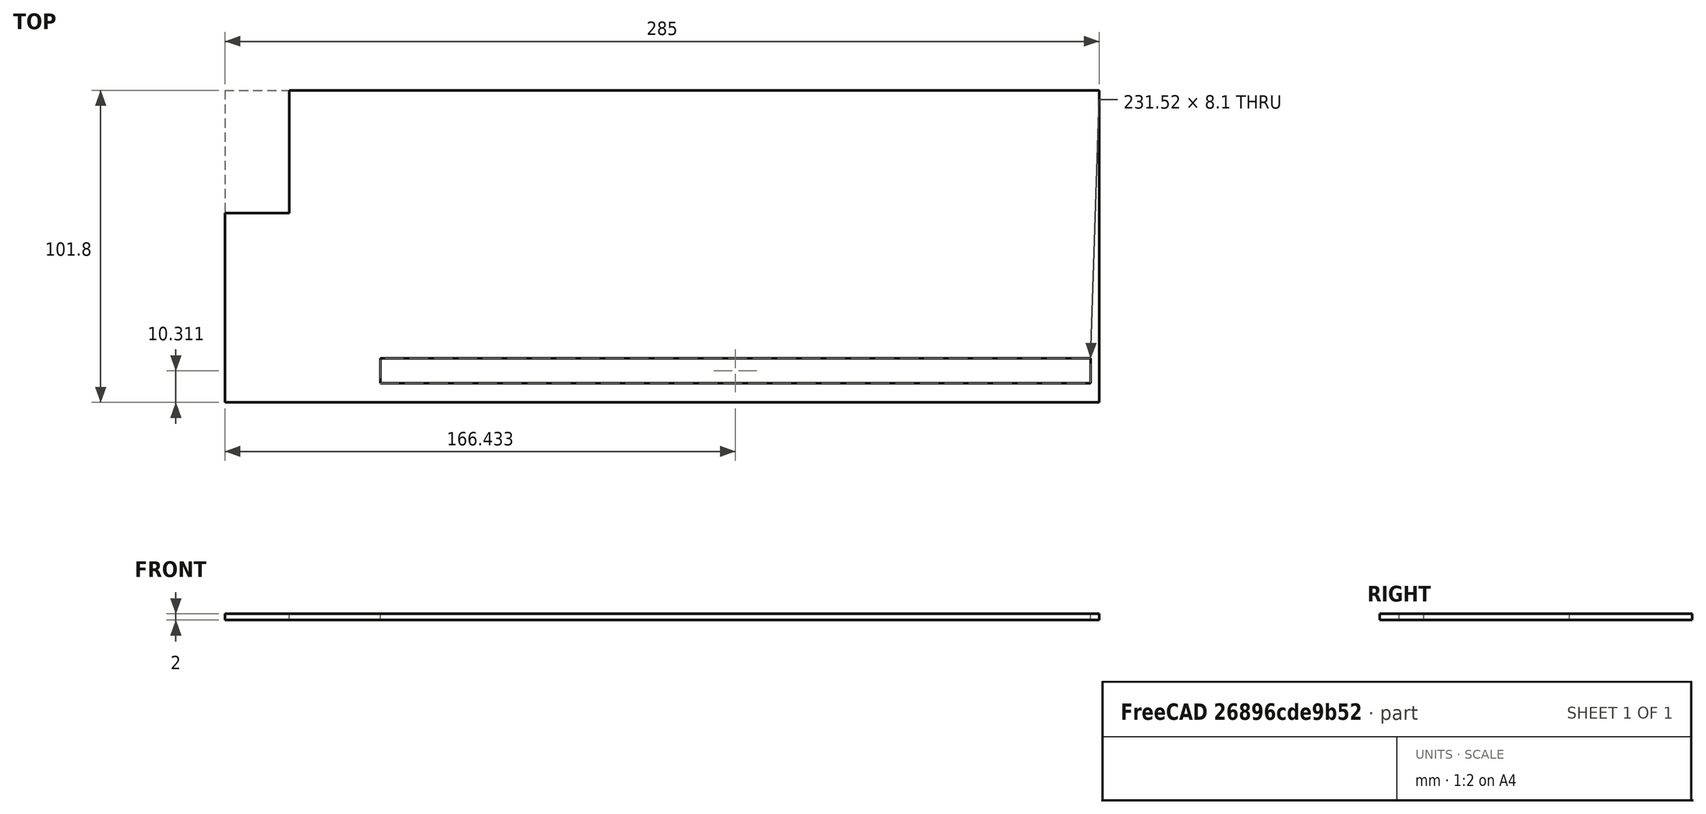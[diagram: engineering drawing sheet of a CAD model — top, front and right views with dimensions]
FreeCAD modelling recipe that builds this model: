
FCSTD DOCUMENT  (FreeCAD 0.20R29603 (Git))
Label: TopPanel
License: All rights reserved
LicenseURL: http://en.wikipedia.org/wiki/All_rights_reserved
objects: Sketcher::SketchObject×1, PartDesign::Pad×1, PartDesign::Body×1
note: 4 computed .brp shape members not serialized (recipe doc carries the construction recipe); baked Part::Feature solids carry a one-line shape summary decoded from their .brp

FEATURE [Sketcher::SketchObject] Sketch
  FullyConstrained = false
  MapMode = 5
  Support = -> [XY_Plane001]
  sketch-geometry (12):
    g0: LineSegment StartX=50.6712 StartY=6.26253 StartZ=0 EndX=50.6757 EndY=14.3625 EndZ=0
    g1: LineSegment StartX=50.6757 StartY=14.3625 StartZ=0 EndX=282.196 EndY=14.3634 EndZ=0
    g2: LineSegment StartX=282.196 StartY=14.3634 StartZ=0 EndX=282.196 EndY=6.25873 EndZ=0
    g3: LineSegment StartX=282.196 StartY=6.25873 StartZ=0 EndX=50.6712 EndY=6.26253 EndZ=0
    g4: LineSegment StartX=2.21647e-09 StartY=101.8 StartZ=0 EndX=21 EndY=101.8 EndZ=0
    g5: LineSegment StartX=21 StartY=101.8 StartZ=0 EndX=21 EndY=61.8 EndZ=0
    g6: LineSegment StartX=21 StartY=61.8 StartZ=0 EndX=2.21647e-09 EndY=61.8 EndZ=0
    g7: LineSegment StartX=2.21647e-09 StartY=61.8 StartZ=0 EndX=2.21647e-09 EndY=101.8 EndZ=0
    g8: LineSegment StartX=0 StartY=0 StartZ=0 EndX=285 EndY=0 EndZ=0
    g9: LineSegment StartX=285 StartY=0 StartZ=0 EndX=285 EndY=101.8 EndZ=0
    g10: LineSegment StartX=285 StartY=101.8 StartZ=0 EndX=0 EndY=101.8 EndZ=0
    g11: LineSegment StartX=0 StartY=101.8 StartZ=0 EndX=0 EndY=0 EndZ=0
  constraints (25):
    c: DistanceY(g0,g0) = 8.1
    c: DistanceX(g1,g1) = 231.52
    c: Coincident(g1,g0)
    c: Coincident(g0,g3)
    c: Coincident(g4,g5)
    c: Coincident(g5,g6)
    c: Coincident(g6,g7)
    c: Coincident(g7,g4)
    c: Horizontal(g4)
    c: Horizontal(g6)
    c: Vertical(g5)
    c: Vertical(g7)
    c: DistanceY(g5,g5) = 40
    c: DistanceX(g6,g6) = 21
    c: Coincident(g8,g9)
    c: Coincident(g9,g10)
    c: Coincident(g10,g11)
    c: Coincident(g11,g8)
    c: Horizontal(g8)
    c: Horizontal(g10)
    c: Vertical(g9)
    c: Vertical(g11)
    c: Coincident(g8,g-1)
    c: DistanceY(g11,g11) = 101.8
    c: DistanceX(g10,g10) = 285
FEATURE [PartDesign::Pad] Pad
  Direction = (0,0,1)
  Length = 2
  Length2 = 10
  Profile = -> Sketch
  ReferenceAxis = -> Sketch [N_Axis]
  Type = 0
FEATURE [PartDesign::Body] Body001
  Group = -> [Sketch,Pad]
  Origin = -> Origin001
  Tip = -> Pad
